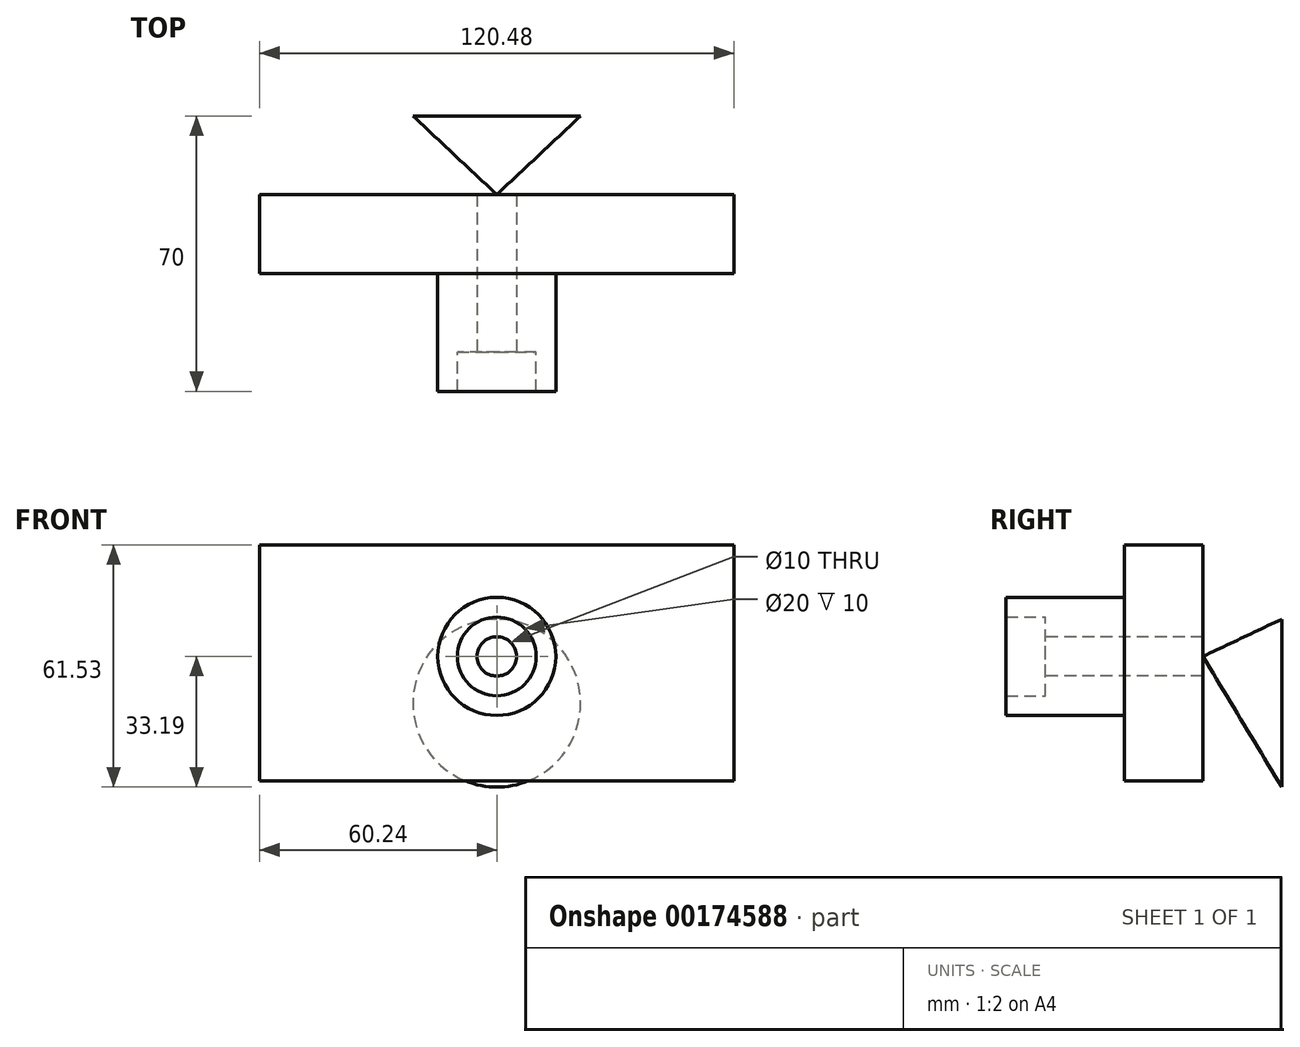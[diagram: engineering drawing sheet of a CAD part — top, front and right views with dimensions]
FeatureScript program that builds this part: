
annotation { "Feature Type Name" : "Feature", "Feature Type Description" : "" }
export const myFeature = defineFeature(function(context is Context, id is Id, definition is map)
    precondition{}
    {
        {
            var Q0;
            Q0=qCreatedBy(makeId("Front.planeOp"),FACE);
            var sketch = newSketch(context, id + "F0", { "sketchPlane" : qUnion([Q0])});
            skLineSegment(sketch, "E0", {"start": v(0, 28.34) * mm, "end": v(0, -31.66) * mm});
            skLineSegment(sketch, "E1", {"start": v(0, -31.66) * mm, "end": v(-45.24, -31.66) * mm});
            skLineSegment(sketch, "E2", {"start": v(-45.24, -31.66) * mm, "end": v(-45.24, 28.34) * mm, "construction": true});
            skLineSegment(sketch, "E3", {"start": v(-45.24, 28.34) * mm, "end": v(0, 28.34) * mm});
            skLineSegment(sketch, "E4", {"start": v(-45.24, -31.66) * mm, "end": v(-50.24, -31.66) * mm});
            skLineSegment(sketch, "E5", {"start": v(-50.24, -31.66) * mm, "end": v(-55.24, -31.66) * mm});
            skLineSegment(sketch, "E6", {"start": v(-55.24, -31.66) * mm, "end": v(-60.24, -31.66) * mm});
            skLineSegment(sketch, "E7", {"start": v(-60.24, -31.66) * mm, "end": v(-60.24, 28.34) * mm});
            skLineSegment(sketch, "E8", {"start": v(-60.24, 28.34) * mm, "end": v(-45.24, 28.34) * mm});
            skLineSegment(sketch, "E9.MirrorCS", {"start": v(45.24, 28.34) * mm, "end": v(0, 28.34) * mm});
            skLineSegment(sketch, "E10.MirrorCS", {"start": v(60.24, 28.34) * mm, "end": v(45.24, 28.34) * mm});
            skLineSegment(sketch, "E11.MirrorCS", {"start": v(60.24, -31.66) * mm, "end": v(60.24, 28.34) * mm});
            skLineSegment(sketch, "E12.MirrorCS", {"start": v(0, -31.66) * mm, "end": v(45.24, -31.66) * mm});
            skLineSegment(sketch, "E13.MirrorCS", {"start": v(50.24, -31.66) * mm, "end": v(55.24, -31.66) * mm});
            skLineSegment(sketch, "E14.MirrorCS", {"start": v(45.24, -31.66) * mm, "end": v(45.24, 28.34) * mm, "construction": true});
            skLineSegment(sketch, "E15.MirrorCS", {"start": v(45.24, -31.66) * mm, "end": v(50.24, -31.66) * mm});
            skLineSegment(sketch, "E16.MirrorCS", {"start": v(55.24, -31.66) * mm, "end": v(60.24, -31.66) * mm});
            skSolve(sketch);
        }
        {
            var Q0;
            Q0 = qSketchRegion(id + "F0", true);
            extrude(context, id + "F1", {"entities" : qUnion([Q0]), "depth" : 20 * mm});
        }
        {
            var Q0;
            Q0=makeQuery(id+"F1.opExtrude","CAP_FACE",FACE,{"disambiguationData":[OSD([sQuery(id+"F0.wireOp",EDGE,"E1"),sQuery(id+"F0.wireOp",EDGE,"E3"),sQuery(id+"F0.wireOp",EDGE,"E4"),sQuery(id+"F0.wireOp",EDGE,"E5"),sQuery(id+"F0.wireOp",EDGE,"E6"),sQuery(id+"F0.wireOp",EDGE,"E7"),sQuery(id+"F0.wireOp",EDGE,"E8"),sQuery(id+"F0.wireOp",EDGE,"E9.MirrorCS"),sQuery(id+"F0.wireOp",EDGE,"E10.MirrorCS"),sQuery(id+"F0.wireOp",EDGE,"E11.MirrorCS"),sQuery(id+"F0.wireOp",EDGE,"E12.MirrorCS"),sQuery(id+"F0.wireOp",EDGE,"E13.MirrorCS"),sQuery(id+"F0.wireOp",EDGE,"E15.MirrorCS"),sQuery(id+"F0.wireOp",EDGE,"E16.MirrorCS")])],"isStart":false});
            var sketch = newSketch(context, id + "F2", { "sketchPlane" : qUnion([Q0])});
            skCircle(sketch, "E17", {"center": v(0, 0) * mm, "radius": 5 * mm});
            skSolve(sketch);
        }
        {
            var Q0;
            Q0=makeQuery(id+"F2.imprint","IMPRINT",FACE,{"disambiguationData":[TD([[makeQuery(id+"F2.imprint","IMPRINT",EDGE,{"derivedFrom":sQuery(id+"F2.wireOp",EDGE,"E17")}),1.0]])]});
            extrude(context, id + "F3", {"entities" : qUnion([Q0]), "operationType" : NewBodyOperationType.REMOVE, "endBound" : BoundingType.THROUGH_ALL, "oppositeDirection" : true, "depth" : 25 * mm});
        }
        {
            var Q0;
            Q0=makeQuery(id+"F1.opExtrude","CAP_FACE",FACE,{"disambiguationData":[OSD([sQuery(id+"F0.wireOp",EDGE,"E1"),sQuery(id+"F0.wireOp",EDGE,"E3"),sQuery(id+"F0.wireOp",EDGE,"E4"),sQuery(id+"F0.wireOp",EDGE,"E5"),sQuery(id+"F0.wireOp",EDGE,"E6"),sQuery(id+"F0.wireOp",EDGE,"E7"),sQuery(id+"F0.wireOp",EDGE,"E8"),sQuery(id+"F0.wireOp",EDGE,"E9.MirrorCS"),sQuery(id+"F0.wireOp",EDGE,"E10.MirrorCS"),sQuery(id+"F0.wireOp",EDGE,"E11.MirrorCS"),sQuery(id+"F0.wireOp",EDGE,"E12.MirrorCS"),sQuery(id+"F0.wireOp",EDGE,"E13.MirrorCS"),sQuery(id+"F0.wireOp",EDGE,"E15.MirrorCS"),sQuery(id+"F0.wireOp",EDGE,"E16.MirrorCS")])],"isStart":false});
            var sketch = newSketch(context, id + "F4", { "sketchPlane" : qUnion([Q0])});
            skCircle(sketch, "E18", {"center": v(0, 0) * mm, "radius": 10 * mm});
            skSolve(sketch);
        }
        {
            var Q0;
            Q0=makeQuery(id+"F4.imprint","IMPRINT",FACE,{"disambiguationData":[TD([[makeQuery(id+"F4.imprint","IMPRINT",EDGE,{"derivedFrom":sQuery(id+"F4.wireOp",EDGE,"E18")}),1.0]])]});
            extrude(context, id + "F5", {"entities" : qUnion([Q0]), "operationType" : NewBodyOperationType.ADD, "depth" : 20 * mm});
        }
        {
            var Q0;
            Q0=makeQuery(id+"F1.opExtrude","CAP_FACE",FACE,{"disambiguationData":[OSD([sQuery(id+"F0.wireOp",EDGE,"E1"),sQuery(id+"F0.wireOp",EDGE,"E3"),sQuery(id+"F0.wireOp",EDGE,"E4"),sQuery(id+"F0.wireOp",EDGE,"E5"),sQuery(id+"F0.wireOp",EDGE,"E6"),sQuery(id+"F0.wireOp",EDGE,"E7"),sQuery(id+"F0.wireOp",EDGE,"E8"),sQuery(id+"F0.wireOp",EDGE,"E9.MirrorCS"),sQuery(id+"F0.wireOp",EDGE,"E10.MirrorCS"),sQuery(id+"F0.wireOp",EDGE,"E11.MirrorCS"),sQuery(id+"F0.wireOp",EDGE,"E12.MirrorCS"),sQuery(id+"F0.wireOp",EDGE,"E13.MirrorCS"),sQuery(id+"F0.wireOp",EDGE,"E15.MirrorCS"),sQuery(id+"F0.wireOp",EDGE,"E16.MirrorCS")])],"isStart":false});
            var sketch = newSketch(context, id + "F6", { "sketchPlane" : qUnion([Q0])});
            skCircle(sketch, "E19", {"center": v(0, 0) * mm, "radius": 15 * mm});
            skSolve(sketch);
        }
        {
            var Q0;
            Q0=makeQuery(id+"F6.imprint","IMPRINT",FACE,{"disambiguationData":[TD([[makeQuery(id+"F6.imprint","IMPRINT",EDGE,{"derivedFrom":sQuery(id+"F6.wireOp",EDGE,"E19")}),1.0]])]});
            var sketch = newSketch(context, id + "F7", { "sketchPlane" : qUnion([Q0])});
            skSolve(sketch);
        }
        {
            var Q0;
            Q0 = qSketchRegion(id + "F7", true);
            var Q1;
            Q1=makeQuery(id+"F6.imprint","IMPRINT",FACE,{"disambiguationData":[TD([[makeQuery(id+"F6.imprint","IMPRINT",EDGE,{"derivedFrom":sQuery(id+"F6.wireOp",EDGE,"E19")}),1.0]])]});
            extrude(context, id + "F8", {"entities" : qUnion([Q0, Q1]), "operationType" : NewBodyOperationType.ADD, "depth" : 30 * mm});
        }
        {
            var Q0;
            Q0=qCreatedBy(makeId("Front.planeOp"),FACE);
            cPlane(context, id + "F9", {"entities" : qUnion([Q0]), "cplaneType" : CPlaneType.OFFSET, "offset" : 20 * mm, "oppositeDirection" : true, "width" : 150 * mm, "height" : 150 * mm});
        }
        {
            var Q0;
            Q0=qCreatedBy(id+"F9.planeOp",FACE);
            var sketch = newSketch(context, id + "F10", { "sketchPlane" : qUnion([Q0])});
            skCircle(sketch, "E20", {"center": v(0, -11.87) * mm, "radius": 21.32 * mm});
            skSolve(sketch);
        }
        {
            var Q0;
            Q0=qCreatedBy(makeId("Origin.pointOp"),VERTEX);
            var Q1;
            Q1=makeQuery(id+"F10.imprint","IMPRINT",FACE,{"disambiguationData":[TD([[makeQuery(id+"F10.imprint","IMPRINT",EDGE,{"derivedFrom":sQuery(id+"F10.wireOp",EDGE,"E20")}),1.0]])]});
            loft(context, id + "F11", {"sheetProfilesArray" : [{ "sheetProfileEntities" : qUnion([Q0]) }, { "sheetProfileEntities" : qUnion([Q1]) }]});
        }
    });
